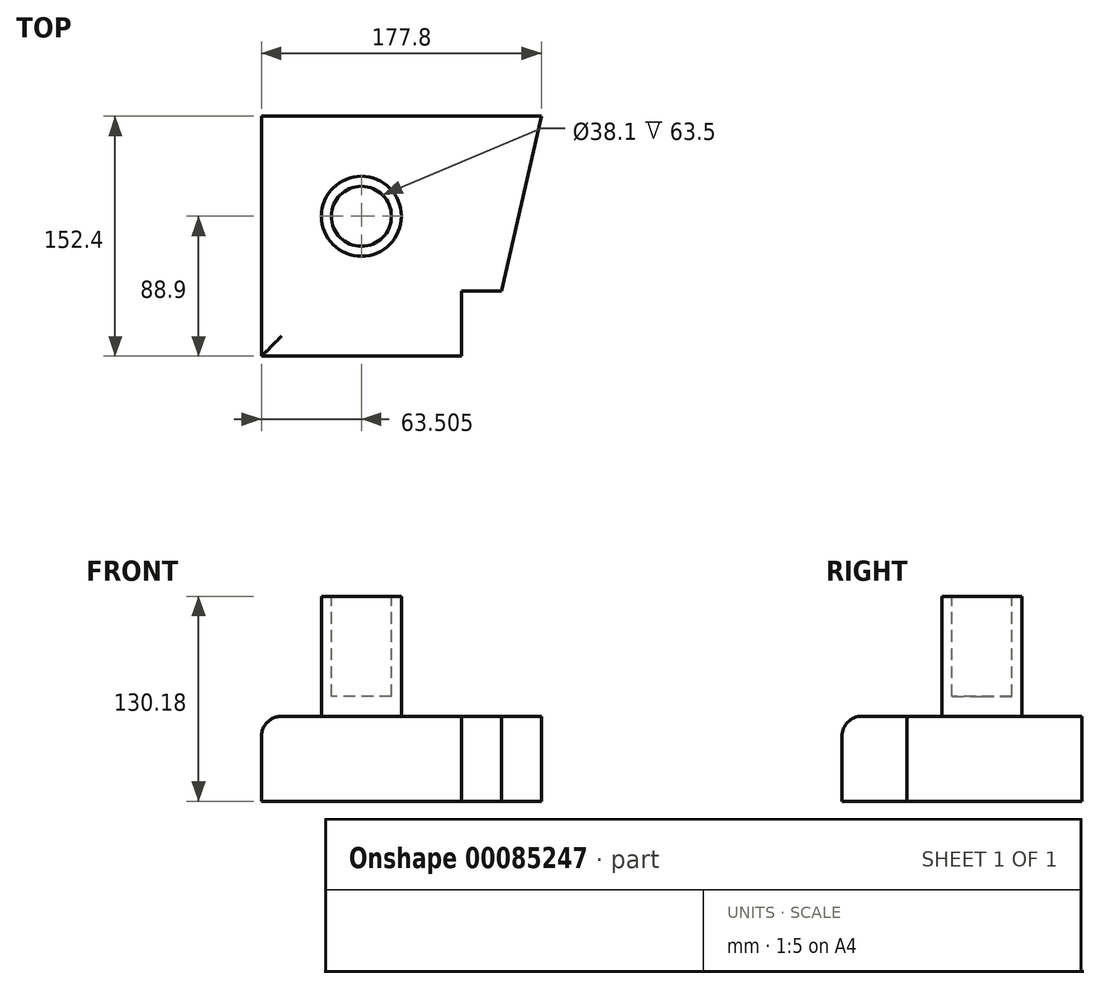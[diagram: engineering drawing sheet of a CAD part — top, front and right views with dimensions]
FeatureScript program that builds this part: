
annotation { "Feature Type Name" : "Feature", "Feature Type Description" : "" }
export const myFeature = defineFeature(function(context is Context, id is Id, definition is map)
    precondition{}
    {
        {
            var Q0;
            Q0=qCreatedBy(makeId("Top.planeOp"),FACE);
            var sketch = newSketch(context, id + "F0", { "sketchPlane" : qUnion([Q0])});
            skLineSegment(sketch, "E0.bottom", {"start": v(-78.52, 81.88) * mm, "end": v(99.28, 81.88) * mm});
            skLineSegment(sketch, "E0.top", {"start": v(-78.52, -70.52) * mm, "end": v(99.28, -70.52) * mm});
            skLineSegment(sketch, "E0.left", {"start": v(-78.52, 81.88) * mm, "end": v(-78.52, -70.52) * mm});
            skLineSegment(sketch, "E0.right", {"start": v(99.28, 81.88) * mm, "end": v(99.28, -70.52) * mm});
            skSolve(sketch);
        }
        {
            var Q0;
            Q0=makeQuery(id+"F0.imprint","IMPRINT",FACE,{"disambiguationData":[TD([[makeQuery(id+"F0.imprint","IMPRINT",EDGE,{"derivedFrom":sQuery(id+"F0.wireOp",EDGE,"E0.bottom")}),-1.0]])]});
            extrude(context, id + "F1", {"entities" : qUnion([Q0]), "depth" : 53.97 * mm});
        }
        {
            var Q0;
            Q0=makeQuery(id+"F1.opExtrude","CAP_FACE",FACE,{"disambiguationData":[OSD([sQuery(id+"F0.wireOp",EDGE,"E0.bottom"),sQuery(id+"F0.wireOp",EDGE,"E0.top"),sQuery(id+"F0.wireOp",EDGE,"E0.left"),sQuery(id+"F0.wireOp",EDGE,"E0.right")])],"isStart":false});
            var sketch = newSketch(context, id + "F2", { "sketchPlane" : qUnion([Q0])});
            skCircle(sketch, "E1", {"center": v(-15.02, 18.38) * mm, "radius": 25.4 * mm});
            skSolve(sketch);
        }
        {
            var Q0;
            Q0=makeQuery(id+"F2.imprint","IMPRINT",FACE,{"disambiguationData":[TD([[makeQuery(id+"F2.imprint","IMPRINT",EDGE,{"derivedFrom":sQuery(id+"F2.wireOp",EDGE,"E1")}),1.0]])]});
            extrude(context, id + "F3", {"entities" : qUnion([Q0]), "operationType" : NewBodyOperationType.ADD, "depth" : 76.2 * mm});
        }
        {
            var Q0;
            Q0=makeQuery(id+"F3.opExtrude","CAP_FACE",FACE,{"disambiguationData":[OSD([sQuery(id+"F2.wireOp",EDGE,"E1")])],"isStart":false});
            var sketch = newSketch(context, id + "F4", { "sketchPlane" : qUnion([Q0])});
            skCircle(sketch, "E2", {"center": v(-15.02, 18.38) * mm, "radius": 19.05 * mm});
            skSolve(sketch);
        }
        {
            var Q0;
            Q0=makeQuery(id+"F4.imprint","IMPRINT",FACE,{"disambiguationData":[TD([[makeQuery(id+"F4.imprint","IMPRINT",EDGE,{"derivedFrom":sQuery(id+"F4.wireOp",EDGE,"E2")}),1.0]])]});
            extrude(context, id + "F5", {"entities" : qUnion([Q0]), "operationType" : NewBodyOperationType.REMOVE, "oppositeDirection" : true, "depth" : 63.5 * mm});
        }
        {
            var Q0;
            Q0=makeQuery(id+"F1.opExtrude","CAP_FACE",FACE,{"disambiguationData":[OSD([sQuery(id+"F0.wireOp",EDGE,"E0.bottom"),sQuery(id+"F0.wireOp",EDGE,"E0.top"),sQuery(id+"F0.wireOp",EDGE,"E0.left"),sQuery(id+"F0.wireOp",EDGE,"E0.right")])],"isStart":false});
            var sketch = newSketch(context, id + "F6", { "sketchPlane" : qUnion([Q0])});
            skLineSegment(sketch, "E3", {"start": v(-78.52, -70.52) * mm, "end": v(48.48, -70.52) * mm});
            skLineSegment(sketch, "E4.bottom", {"start": v(48.48, -70.52) * mm, "end": v(73.88, -70.52) * mm});
            skLineSegment(sketch, "E4.top", {"start": v(48.48, -29.24) * mm, "end": v(73.88, -29.24) * mm});
            skLineSegment(sketch, "E4.left", {"start": v(48.48, -70.52) * mm, "end": v(48.48, -29.24) * mm});
            skLineSegment(sketch, "E4.right", {"start": v(73.88, -70.52) * mm, "end": v(73.88, -29.24) * mm});
            skSolve(sketch);
        }
        {
            var Q0;
            Q0=makeQuery(id+"F6.imprint","IMPRINT",FACE,{"disambiguationData":[TD([[makeQuery(id+"F6.imprint","IMPRINT",EDGE,{"derivedFrom":sQuery(id+"F6.wireOp",EDGE,"E4.bottom")}),1.0]])]});
            extrude(context, id + "F7", {"entities" : qUnion([Q0]), "operationType" : NewBodyOperationType.REMOVE, "oppositeDirection" : true, "depth" : 60.3 * mm});
        }
        {
            var Q0;
            Q0=makeQuery(id+"F1.opExtrude","CAP_FACE",FACE,{"disambiguationData":[OSD([sQuery(id+"F0.wireOp",EDGE,"E0.bottom"),sQuery(id+"F0.wireOp",EDGE,"E0.top"),sQuery(id+"F0.wireOp",EDGE,"E0.left"),sQuery(id+"F0.wireOp",EDGE,"E0.right")])],"isStart":false});
            var sketch = newSketch(context, id + "F8", { "sketchPlane" : qUnion([Q0])});
            skLineSegment(sketch, "E5", {"start": v(73.88, -29.24) * mm, "end": v(99.28, 81.88) * mm});
            skSolve(sketch);
        }
        {
            var Q0;
            Q0=makeQuery(id+"F8.imprint","IMPRINT",FACE,{"disambiguationData":[TD([[makeQuery(id+"F8.imprint","IMPRINT",EDGE,{"derivedFrom":sQuery(id+"F8.wireOp",EDGE,"E5")}),-1.0]])]});
            extrude(context, id + "F9", {"entities" : qUnion([Q0]), "operationType" : NewBodyOperationType.REMOVE, "oppositeDirection" : true, "depth" : 62.03 * mm});
        }
        {
            var Q0;
            Q0=makeQuery(id+"F3.opExtrude","CAP_EDGE",EDGE,{"disambiguationData":[OSD([sQuery(id+"F2.wireOp",EDGE,"E1")])],"isStart":true});
            var Q1;
            {var subQ0=sQuery(id+"F0.wireOp",EDGE,"E0.left");var subQ1=sQuery(id+"F0.wireOp",EDGE,"E0.top");Q1=makeQuery(id+"F7.boolean.opBoolean","SPLIT",EDGE,{"disambiguationData":[TD([makeQuery(id+"F1.opExtrude","SWEPT_FACE",FACE,{"disambiguationData":[OSD([subQ0])]})])],"derivedFrom":makeQuery(id+"F1.opExtrude","CAP_EDGE",EDGE,{"disambiguationData":[OSD([subQ1])],"isStart":false})});}
            var Q2;
            Q2=makeQuery(id+"F7.boolean.opBoolean","COPY",EDGE,{"derivedFrom":makeQuery(id+"F7.opExtrude","CAP_EDGE",EDGE,{"disambiguationData":[OSD([sQuery(id+"F6.wireOp",EDGE,"E4.left")])],"isStart":true})});
            var Q3;
            Q3=makeQuery(id+"F1.opExtrude","CAP_EDGE",EDGE,{"disambiguationData":[OSD([sQuery(id+"F0.wireOp",EDGE,"E0.left")])],"isStart":false});
            fillet(context, id + "F10", {"entities" : qUnion([Q0, Q1, Q2, Q3]), "radius" : 12.7 * mm, "tangentPropagation" : true, "allowEdgeOverflow" : false});
        }
    });
